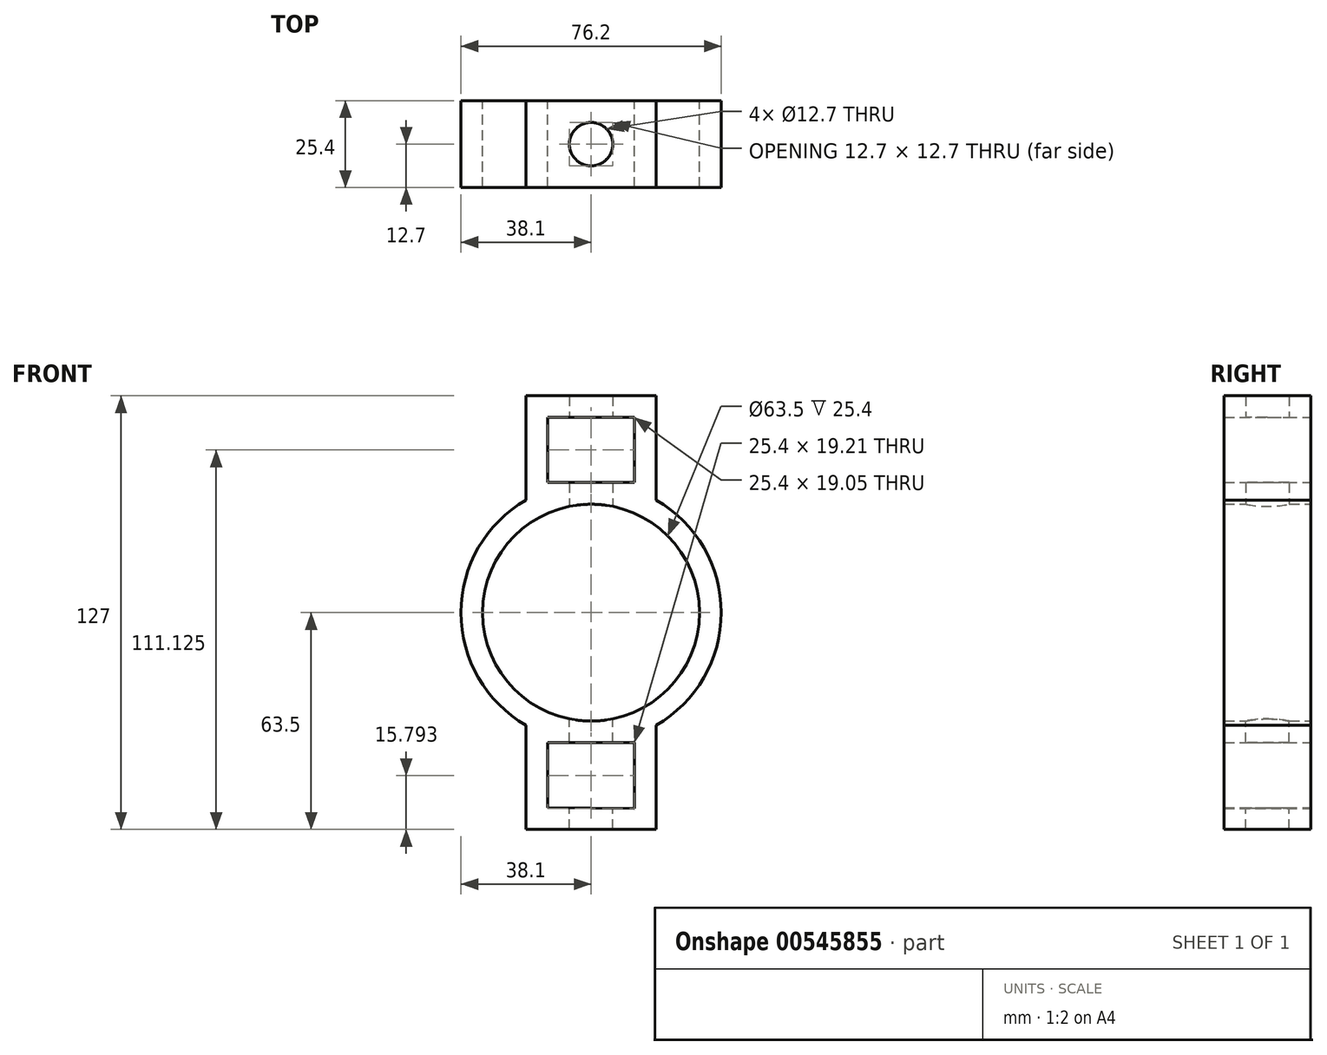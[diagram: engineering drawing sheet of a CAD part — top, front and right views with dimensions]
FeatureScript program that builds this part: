
annotation { "Feature Type Name" : "Feature", "Feature Type Description" : "" }
export const myFeature = defineFeature(function(context is Context, id is Id, definition is map)
    precondition{}
    {
        {
            var Q0;
            Q0=qCreatedBy(makeId("Front.planeOp"),FACE);
            var sketch = newSketch(context, id + "F0", { "sketchPlane" : qUnion([Q0])});
            skCircle(sketch, "E0", {"center": v(0, 0) * mm, "radius": 31.75 * mm});
            skCircle(sketch, "E1", {"center": v(0, 0) * mm, "radius": 38.1 * mm});
            skLineSegment(sketch, "E2", {"start": v(-19.05, 38.1) * mm, "end": v(19.05, 38.1) * mm});
            skLineSegment(sketch, "E3", {"start": v(19.05, 38.1) * mm, "end": v(19.05, 33) * mm});
            skLineSegment(sketch, "E4", {"start": v(-19.05, 38.1) * mm, "end": v(-19.05, 33) * mm});
            skLineSegment(sketch, "E5", {"start": v(-19.05, 38.1) * mm, "end": v(-19.05, 44.45) * mm});
            skLineSegment(sketch, "E6", {"start": v(19.05, 38.1) * mm, "end": v(19.05, 44.45) * mm});
            skLineSegment(sketch, "E7", {"start": v(-19.05, 44.45) * mm, "end": v(-12.7, 44.45) * mm});
            skLineSegment(sketch, "E8", {"start": v(19.05, 44.45) * mm, "end": v(12.7, 44.45) * mm});
            skLineSegment(sketch, "E9", {"start": v(-12.7, 44.45) * mm, "end": v(-12.7, 38.1) * mm});
            skLineSegment(sketch, "E10", {"start": v(12.7, 44.45) * mm, "end": v(12.7, 38.1) * mm});
            skLineSegment(sketch, "E11.0", {"start": v(-19.05, -38.1) * mm, "end": v(19.05, -38.1) * mm});
            skLineSegment(sketch, "E12", {"start": v(19.05, -38.1) * mm, "end": v(19.05, -33) * mm});
            skLineSegment(sketch, "E13", {"start": v(-19.05, -38.1) * mm, "end": v(-19.05, -33) * mm});
            skLineSegment(sketch, "E14", {"start": v(-19.05, -38.1) * mm, "end": v(-19.05, -44.45) * mm});
            skLineSegment(sketch, "E15", {"start": v(19.05, -38.1) * mm, "end": v(19.05, -44.61) * mm});
            skLineSegment(sketch, "E16", {"start": v(19.05, -44.61) * mm, "end": v(12.7, -44.61) * mm});
            skLineSegment(sketch, "E17", {"start": v(-19.05, -44.45) * mm, "end": v(-12.7, -44.45) * mm});
            skLineSegment(sketch, "E18", {"start": v(12.7, -44.61) * mm, "end": v(12.7, -38.1) * mm});
            skLineSegment(sketch, "E19", {"start": v(-12.7, -44.45) * mm, "end": v(-12.7, -38.1) * mm});
            skLineSegment(sketch, "E20", {"start": v(-19.05, -44.45) * mm, "end": v(-19.05, -63.5) * mm});
            skLineSegment(sketch, "E21", {"start": v(19.05, -44.61) * mm, "end": v(19.05, -63.5) * mm});
            skLineSegment(sketch, "E22", {"start": v(-19.05, -63.5) * mm, "end": v(19.05, -63.5) * mm});
            skLineSegment(sketch, "E23", {"start": v(-12.7, -44.45) * mm, "end": v(-12.7, -57.15) * mm});
            skLineSegment(sketch, "E24", {"start": v(12.7, -44.61) * mm, "end": v(12.7, -57.31) * mm});
            skLineSegment(sketch, "E25", {"start": v(-12.7, -57.15) * mm, "end": v(12.7, -57.31) * mm});
            skLineSegment(sketch, "E26", {"start": v(-19.05, 44.45) * mm, "end": v(-19.05, 63.5) * mm});
            skLineSegment(sketch, "E27", {"start": v(19.05, 44.45) * mm, "end": v(19.05, 63.5) * mm});
            skLineSegment(sketch, "E28", {"start": v(-12.7, 44.45) * mm, "end": v(-12.7, 57.15) * mm});
            skLineSegment(sketch, "E29", {"start": v(12.7, 44.45) * mm, "end": v(12.7, 57.15) * mm});
            skLineSegment(sketch, "E30", {"start": v(-12.7, 57.15) * mm, "end": v(12.7, 57.15) * mm});
            skLineSegment(sketch, "E31", {"start": v(19.05, 63.5) * mm, "end": v(-19.05, 63.5) * mm});
            skSolve(sketch);
        }
        {
            var Q0;
            Q0 = qSketchRegion(id + "F0", true);
            extrude(context, id + "F1", {"entities" : qUnion([Q0]), "depth" : 25.4 * mm, "offsetDistance" : 25.4 * mm});
        }
        {
            var Q0;
            Q0=qCreatedBy(makeId("Top.planeOp"),FACE);
            var sketch = newSketch(context, id + "F2", { "sketchPlane" : qUnion([Q0])});
            skLineSegment(sketch, "E32", {"start": v(0, 0) * mm, "end": v(0, -12.7) * mm});
            skCircle(sketch, "E33", {"center": v(0, -12.7) * mm, "radius": 6.35 * mm});
            skSolve(sketch);
        }
        {
            var Q0;
            Q0 = qSketchRegion(id + "F2", true);
            var Q1;
            Q1=sQuery(id+"F2.wireOp",EDGE,"E32");
            extrude(context, id + "F3", {"entities" : qUnion([Q0]), "operationType" : NewBodyOperationType.REMOVE, "surfaceEntities" : qUnion([Q1]), "oppositeDirection" : true, "depth" : 102.1 * mm, "offsetDistance" : 25.4 * mm});
        }
        {
            var Q0;
            Q0 = qSketchRegion(id + "F2", true);
            extrude(context, id + "F4", {"entities" : qUnion([Q0]), "operationType" : NewBodyOperationType.REMOVE, "depth" : 65.28 * mm, "offsetDistance" : 25.4 * mm});
        }
    });
